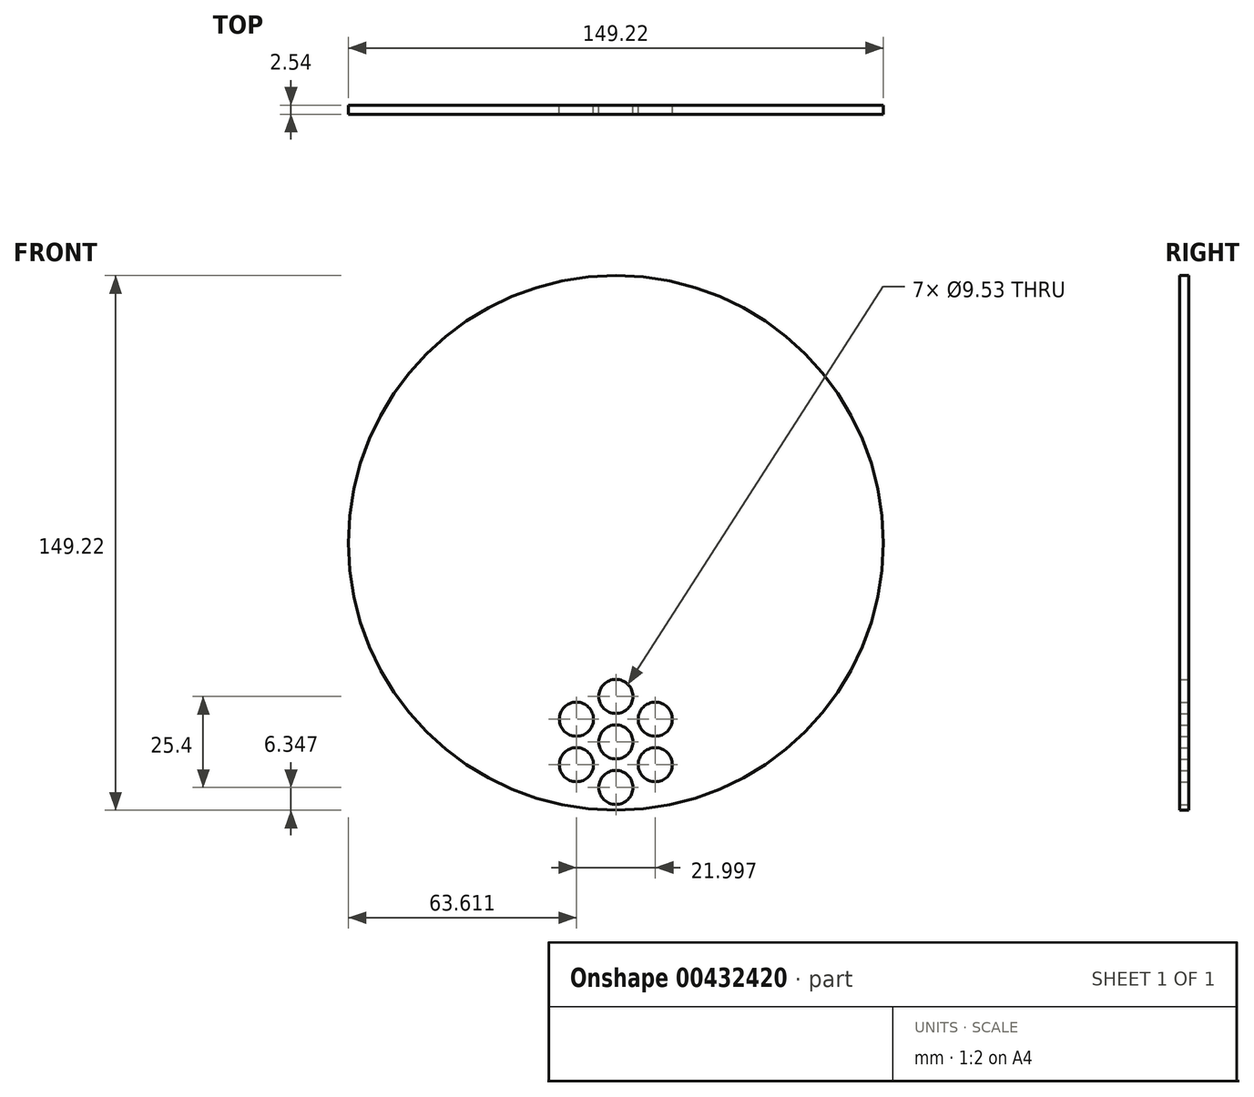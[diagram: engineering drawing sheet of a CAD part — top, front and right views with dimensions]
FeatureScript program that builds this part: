
annotation { "Feature Type Name" : "Feature", "Feature Type Description" : "" }
export const myFeature = defineFeature(function(context is Context, id is Id, definition is map)
    precondition{}
    {
        {
            var Q0;
            Q0=qCreatedBy(makeId("Front.planeOp"),FACE);
            var sketch = newSketch(context, id + "F0", { "sketchPlane" : qUnion([Q0])});
            skCircle(sketch, "E0", {"center": v(0, 0) * mm, "radius": 74.61 * mm});
            skLineSegment(sketch, "E1", {"start": v(0, 0) * mm, "end": v(0, -74.61) * mm});
            skLineSegment(sketch, "E2", {"start": v(0, -74.61) * mm, "end": v(0, -55.56) * mm});
            skLineSegment(sketch, "E3", {"start": v(0, -55.56) * mm, "end": v(0, -68.26) * mm});
            skCircle(sketch, "E4", {"center": v(0, -68.26) * mm, "radius": 4.76 * mm});
            skCircle(sketch, "E5.1.0", {"center": v(11, -61.91) * mm, "radius": 4.76 * mm});
            skCircle(sketch, "E5.2.0", {"center": v(11, -49.21) * mm, "radius": 4.76 * mm});
            skCircle(sketch, "E5.3.0", {"center": v(0, -42.86) * mm, "radius": 4.76 * mm});
            skCircle(sketch, "E5.4.0", {"center": v(-11, -49.21) * mm, "radius": 4.76 * mm});
            skCircle(sketch, "E5.5.0", {"center": v(-11, -61.91) * mm, "radius": 4.76 * mm});
            skPoint(sketch, "E5.center", {"position": v(0, -55.56) * mm});
            skCircle(sketch, "E6", {"center": v(0, -55.56) * mm, "radius": 4.76 * mm});
            skSolve(sketch);
        }
        {
            var Q0;
            Q0 = qSketchRegion(id + "F0", true);
            extrude(context, id + "F1", {"entities" : qUnion([Q0]), "depth" : 2.54 * mm});
        }
    });
